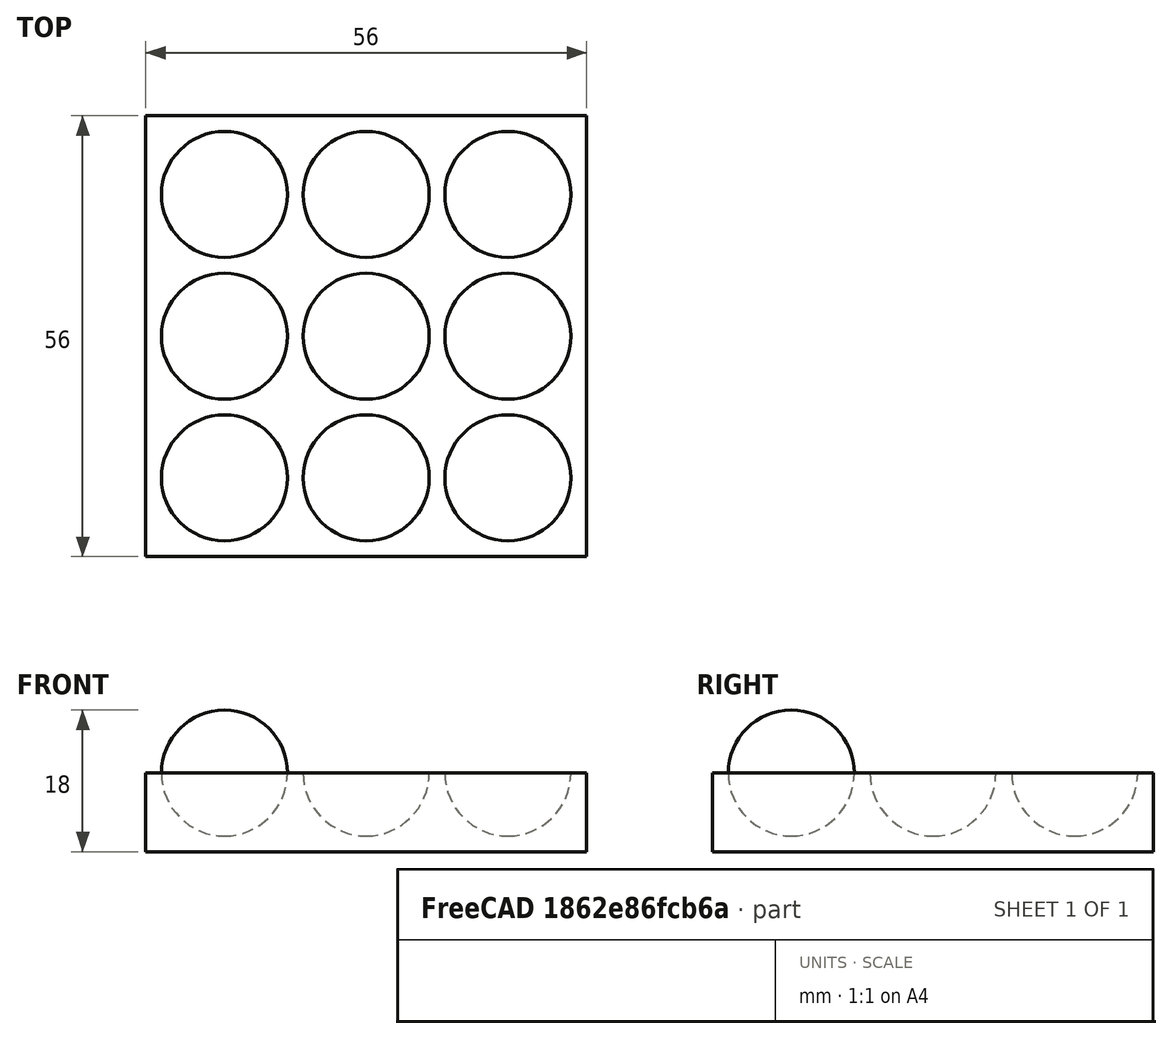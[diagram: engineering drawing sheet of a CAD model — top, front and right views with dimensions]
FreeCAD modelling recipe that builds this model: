
FCSTD DOCUMENT  (FreeCAD 0.21R33694 (Git))
Label: OJT1_T013_canicas
License: All rights reserved
LicenseURL: https://en.wikipedia.org/wiki/All_rights_reserved
objects: Part::Sphere×1, Part::FeaturePython×1, Part::Box×1, Part::Cut×1
note: 3 computed .brp shape members not serialized (recipe doc carries the construction recipe); baked Part::Feature solids carry a one-line shape summary decoded from their .brp

FEATURE [Part::Sphere] Sphere  label="Esfera"
  Angle1 = -90
  Angle2 = 90
  Angle3 = 360
  AttacherType = Attacher::AttachEngine3D
  Radius = 8
FEATURE [Part::FeaturePython] Array  # Draft array (typed FeaturePython)
  AlwaysSyncPlacement = false
  Angle = 360
  ArrayType = 0
  Axis = (0,0,1)
  Base = -> Sphere
  Center = (0,0,0)
  Count = 9
  ExpandArray = false
  Fuse = false
  IntervalAxis = (0,0,0)
  IntervalX = (18,0,0)
  IntervalY = (0,18,0)
  IntervalZ = (0,0,100)
  NumberCircles = 3
  NumberPolar = 5
  NumberX = 3
  NumberY = 3
  NumberZ = 1
  PlacementList = 9 placements: [(0,0,0),(0,18,0),(0,36,0),(18,0,0),(18,18,0),(18,36,0),(36,0,0),(36,18,0),(36,36,0)]
  RadialDistance = 50
  ScaleList = (9) [(1,1,1),(1,1,1),(1,1,1),(1,1,1),(1,1,1),(1,1,1),(1,1,1),(1,1,1),(1,1,1)]
  Symmetry = 1
  TangentialDistance = 25
FEATURE [Part::Box] Box  label="Cub"
  AttacherType = Attacher::AttachEngine3D
  Height = 10
  Length = 56
  Placement = pos=(-10,-10,-10) rot=(0,0,1;0rad)
  Width = 56
  expr: .Placement.Base.x = -10
  expr: .Placement.Base.y = -10
  expr: .Placement.Base.z = -10
FEATURE [Part::Cut] Cut
  Base = -> Box
  Tool = -> Array
